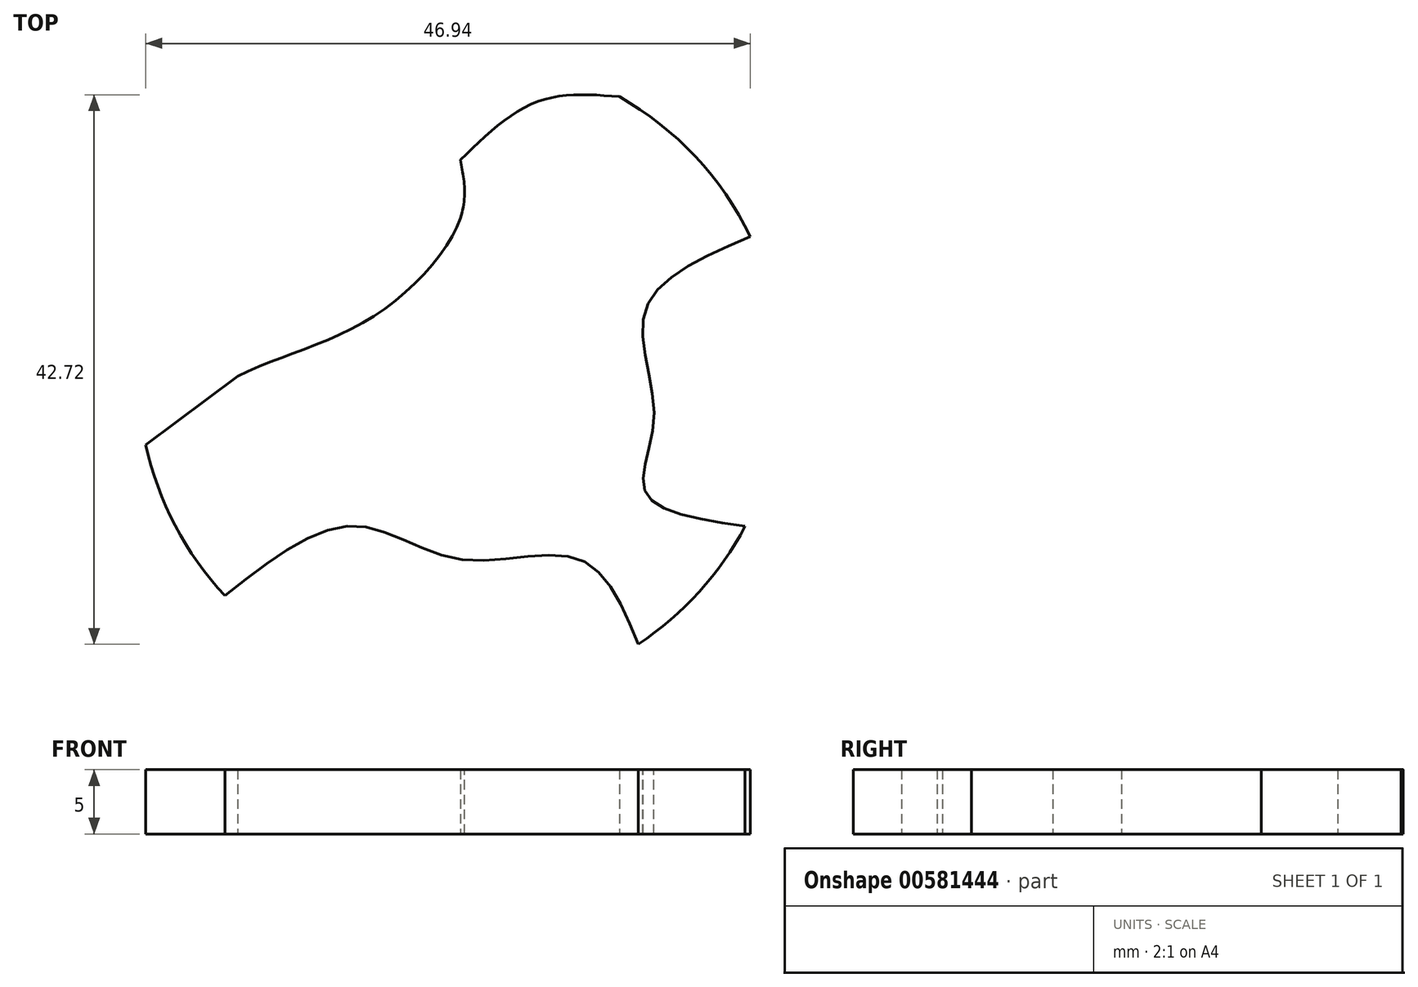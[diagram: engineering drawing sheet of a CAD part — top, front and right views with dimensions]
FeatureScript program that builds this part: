
annotation { "Feature Type Name" : "Feature", "Feature Type Description" : "" }
export const myFeature = defineFeature(function(context is Context, id is Id, definition is map)
    precondition{}
    {
        {
            var Q0;
            Q0=qCreatedBy(makeId("Top.planeOp"),FACE);
            var sketch = newSketch(context, id + "F0", { "sketchPlane" : qUnion([Q0])});
            skCircle(sketch, "E0", {"center": v(0, 0) * mm, "radius": 25 * mm});
            skLineSegment(sketch, "E1", {"start": v(-24.43, -5.32) * mm, "end": v(-17.3, 0) * mm});
            skLineSegment(sketch, "E2", {"start": v(0, 16.82) * mm, "end": v(0, 12.29) * mm});
            skFitSpline(sketch, "E3", {"points": [v(-24.43, -5.32) * mm, v(-17.3, 0) * mm, v(-6.95, 4.53) * mm, v(0, 12.29) * mm, v(0, 16.82) * mm], "startDerivative": vector(25.68, 23.1) * mm, "endDerivative": vector(-4.7, 23.42) * mm});
            skFitSpline(sketch, "E4", {"points": [v(0, 16.82) * mm, v(5.98, 21.34) * mm, v(12.35, 21.74) * mm], "startDerivative": vector(11.04, 10.75) * mm, "endDerivative": vector(13.68, -1.08) * mm});
            skFitSpline(sketch, "E5", {"points": [v(22.51, 10.87) * mm, v(14.4, 5.17) * mm, v(15.04, -3.23) * mm, v(14.4, -9.06) * mm, v(22.12, -11.65) * mm], "startDerivative": vector(-39.1, -16.9) * mm, "endDerivative": vector(41.16, -6) * mm});
            skFitSpline(sketch, "E6", {"points": [v(-18.27, -17.06) * mm, v(-8.25, -11.64) * mm, v(0, -14.23) * mm, v(9.22, -14.23) * mm, v(13.83, -20.83) * mm], "startDerivative": vector(37.27, 29.47) * mm, "endDerivative": vector(15.08, -36.88) * mm});
            skSolve(sketch);
        }
        {
            var Q0;
            {var subQ0=sQuery(id+"F0.wireOp",EDGE,"E1");Q0=makeQuery(id+"F0.imprint","IMPRINT",FACE,{"disambiguationData":[TD([[makeQuery(id+"F0.imprint","IMPRINT",EDGE,{"derivedFrom":subQ0}),-1.0]])]});}
            extrude(context, id + "F1", {"entities" : qUnion([Q0]), "depth" : 5 * mm, "offsetDistance" : 25 * mm});
        }
    });
